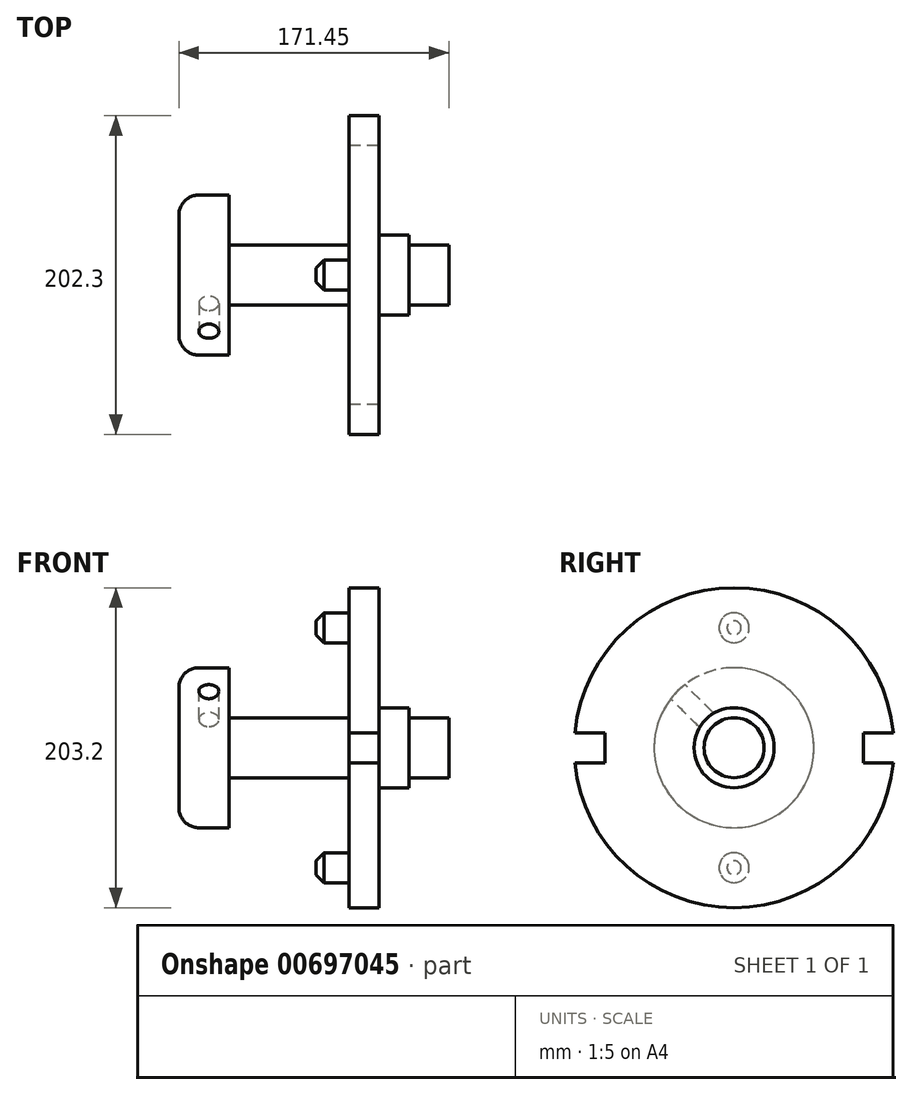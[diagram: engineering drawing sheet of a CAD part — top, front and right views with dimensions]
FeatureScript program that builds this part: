
annotation { "Feature Type Name" : "Feature", "Feature Type Description" : "" }
export const myFeature = defineFeature(function(context is Context, id is Id, definition is map)
    precondition{}
    {
        {
            var Q0;
            Q0=qCreatedBy(makeId("Front.planeOp"),FACE);
            var sketch = newSketch(context, id + "F0", { "sketchPlane" : qUnion([Q0])});
            skLineSegment(sketch, "E0", {"start": v(-314.96, 0) * mm, "end": v(248.68, 0) * mm, "construction": true});
            skLineSegment(sketch, "E1", {"start": v(0, 0) * mm, "end": v(0, 19.05) * mm});
            skLineSegment(sketch, "E2", {"start": v(0, 19.05) * mm, "end": v(-25.4, 19.05) * mm});
            skLineSegment(sketch, "E3", {"start": v(-25.4, 19.05) * mm, "end": v(-25.4, 25.4) * mm});
            skLineSegment(sketch, "E4", {"start": v(-25.4, 25.4) * mm, "end": v(-44.45, 25.4) * mm});
            skLineSegment(sketch, "E5", {"start": v(-44.45, 25.4) * mm, "end": v(-44.45, 101.6) * mm});
            skLineSegment(sketch, "E6", {"start": v(-44.45, 101.6) * mm, "end": v(-63.5, 101.6) * mm});
            skLineSegment(sketch, "E7", {"start": v(-63.5, 101.6) * mm, "end": v(-63.5, 19.05) * mm});
            skLineSegment(sketch, "E8", {"start": v(-63.5, 19.05) * mm, "end": v(-139.7, 19.05) * mm});
            skLineSegment(sketch, "E9", {"start": v(-139.7, 19.05) * mm, "end": v(-139.7, 50.8) * mm});
            skLineSegment(sketch, "E10", {"start": v(-139.7, 50.8) * mm, "end": v(-158.75, 50.8) * mm});
            skLineSegment(sketch, "E11", {"start": v(-171.45, 38.1) * mm, "end": v(-171.45, 0) * mm});
            skPoint(sketch, "E12.visualSharp", {"position": v(-171.45, 50.8) * mm});
            skArc(sketch, "E12.filletArc", {"start": v(-158.75, 50.8) * mm, "mid": v(-167.73, 47.08) * mm, "end": v(-171.45, 38.1) * mm});
            skLineSegment(sketch, "E13", {"start": v(-171.45, 0) * mm, "end": v(0, 0) * mm});
            skSolve(sketch);
        }
        {
            var Q0;
            Q0=makeQuery(id+"F0.imprint","IMPRINT",FACE,{"disambiguationData":[TD([[makeQuery(id+"F0.imprint","IMPRINT",EDGE,{"derivedFrom":sQuery(id+"F0.wireOp",EDGE,"E1")}),1.0]])]});
            var Q1;
            Q1=sQuery(id+"F0.wireOp",EDGE,"E0");
            revolve(context, id + "F1", {"entities" : qUnion([Q0]), "axis" : qUnion([Q1]), "revolveType" : RevolveType.FULL});
        }
        {
            var Q0;
            Q0=makeQuery(id+"F1.opRevolve","SWEPT_FACE",FACE,{"disambiguationData":[OSD([sQuery(id+"F0.wireOp",EDGE,"E7")])]});
            var sketch = newSketch(context, id + "F2", { "sketchPlane" : qUnion([Q0])});
            skLineSegment(sketch, "E14", {"start": v(0, 101.6) * mm, "end": v(0, -101.6) * mm, "construction": true});
            skCircle(sketch, "E15", {"center": v(0, 76.2) * mm, "radius": 9.53 * mm});
            skSolve(sketch);
        }
        {
            var Q0;
            Q0=makeQuery(id+"F2.imprint","IMPRINT",FACE,{"disambiguationData":[TD([[makeQuery(id+"F2.imprint","IMPRINT",EDGE,{"derivedFrom":sQuery(id+"F2.wireOp",EDGE,"E15")}),1.0]])]});
            extrude(context, id + "F3", {"entities" : qUnion([Q0]), "operationType" : NewBodyOperationType.ADD, "depth" : 20.83 * mm});
        }
        {
            var Q0;
            Q0=makeQuery(id+"F3.opExtrude","CAP_EDGE",EDGE,{"disambiguationData":[OSD([sQuery(id+"F2.wireOp",EDGE,"E15")])],"isStart":false});
            chamfer(context, id + "F4", {"entities" : qUnion([Q0]), "width" : 5.08 * mm, "tangentPropagation" : true});
        }
        {
            var Q0;
            Q0=makeQuery(id+"F1.opRevolve","SWEPT_FACE",FACE,{"disambiguationData":[OSD([sQuery(id+"F0.wireOp",EDGE,"E7")])]});
            var sketch = newSketch(context, id + "F5", { "sketchPlane" : qUnion([Q0])});
            skLineSegment(sketch, "E16", {"start": v(0, -101.6) * mm, "end": v(0, 0) * mm, "construction": true});
            skCircle(sketch, "E17", {"center": v(0, -76.2) * mm, "radius": 9.53 * mm});
            skSolve(sketch);
        }
        {
            var Q0;
            Q0=makeQuery(id+"F5.imprint","IMPRINT",FACE,{"disambiguationData":[TD([[makeQuery(id+"F5.imprint","IMPRINT",EDGE,{"derivedFrom":sQuery(id+"F5.wireOp",EDGE,"E17")}),1.0]])]});
            extrude(context, id + "F6", {"entities" : qUnion([Q0]), "operationType" : NewBodyOperationType.ADD, "depth" : 20.83 * mm});
        }
        {
            var Q0;
            Q0=makeQuery(id+"F6.opExtrude","CAP_EDGE",EDGE,{"disambiguationData":[OSD([sQuery(id+"F5.wireOp",EDGE,"E17")])],"isStart":false});
            chamfer(context, id + "F7", {"entities" : qUnion([Q0]), "width" : 5.08 * mm, "tangentPropagation" : true});
        }
        {
            var Q0;
            Q0=makeQuery(id+"F1.opRevolve","SWEPT_FACE",FACE,{"disambiguationData":[OSD([sQuery(id+"F0.wireOp",EDGE,"E7")])]});
            var sketch = newSketch(context, id + "F8", { "sketchPlane" : qUnion([Q0])});
            skLineSegment(sketch, "E18", {"start": v(-101.6, 0) * mm, "end": v(0, 0) * mm, "construction": true});
            skLineSegment(sketch, "E19", {"start": v(-101.15, 9.53) * mm, "end": v(-82.1, 9.53) * mm});
            skLineSegment(sketch, "E20", {"start": v(-82.1, 9.53) * mm, "end": v(-82.1, -9.53) * mm});
            skLineSegment(sketch, "E21", {"start": v(-82.1, -9.53) * mm, "end": v(-101.15, -9.53) * mm});
            skSolve(sketch);
        }
        {
            var Q0;
            {var subQ0=sQuery(id+"F8.wireOp",EDGE,"E19");Q0=makeQuery(id+"F8.imprint","IMPRINT",FACE,{"disambiguationData":[TD([[makeQuery(id+"F8.imprint","IMPRINT",EDGE,{"derivedFrom":subQ0}),-1.0]])]});}
            extrude(context, id + "F9", {"entities" : qUnion([Q0]), "operationType" : NewBodyOperationType.REMOVE, "oppositeDirection" : true, "depth" : 25.4 * mm});
        }
        {
            var Q0;
            Q0=makeQuery(id+"F1.opRevolve","SWEPT_FACE",FACE,{"disambiguationData":[OSD([sQuery(id+"F0.wireOp",EDGE,"E7")])]});
            var sketch = newSketch(context, id + "F10", { "sketchPlane" : qUnion([Q0])});
            skLineSegment(sketch, "E22", {"start": v(0, 0) * mm, "end": v(101.6, 0) * mm, "construction": true});
            skLineSegment(sketch, "E23", {"start": v(101.15, 9.53) * mm, "end": v(82.1, 9.53) * mm});
            skLineSegment(sketch, "E24", {"start": v(82.1, 9.53) * mm, "end": v(82.1, -9.52) * mm});
            skLineSegment(sketch, "E25", {"start": v(82.1, -9.52) * mm, "end": v(101.6, -9.52) * mm});
            skSolve(sketch);
        }
        {
            var Q0;
            {var subQ0=sQuery(id+"F10.wireOp",EDGE,"E23");Q0=makeQuery(id+"F10.imprint","IMPRINT",FACE,{"disambiguationData":[TD([[makeQuery(id+"F10.imprint","IMPRINT",EDGE,{"derivedFrom":subQ0}),1.0]])]});}
            extrude(context, id + "F11", {"entities" : qUnion([Q0]), "operationType" : NewBodyOperationType.REMOVE, "oppositeDirection" : true, "depth" : 25.4 * mm});
        }
        {
            var Q0;
            Q0=makeQuery(id+"F1.opRevolve","SWEPT_FACE",FACE,{"disambiguationData":[OSD([sQuery(id+"F0.wireOp",EDGE,"E9")])]});
            var sketch = newSketch(context, id + "F12", { "sketchPlane" : qUnion([Q0])});
            skLineSegment(sketch, "E26", {"start": v(0, 0) * mm, "end": v(-35.92, 35.92) * mm});
            skLineSegment(sketch, "E27", {"start": v(0, -64.38) * mm, "end": v(0, 24.9) * mm});
            skSolve(sketch);
        }
        {
            var Q0;
            Q0=sQuery(id+"F12.wireOp",VERTEX,"E26.end");
            var Q1;
            Q1=sQuery(id+"F12.wireOp",EDGE,"E26");
            cPlane(context, id + "F13", {"entities" : qUnion([Q0, Q1]), "cplaneType" : CPlaneType.LINE_POINT, "offset" : 25.4 * mm, "width" : 152.4 * mm, "height" : 152.4 * mm});
        }
        {
            var Q0;
            Q0=qCreatedBy(id+"F13.planeOp",FACE);
            var sketch = newSketch(context, id + "F14", { "sketchPlane" : qUnion([Q0])});
            skCircle(sketch, "E28", {"center": v(-152.4, 0) * mm, "radius": 6.35 * mm});
            skSolve(sketch);
        }
        {
            var Q0;
            Q0=makeQuery(id+"F14.imprint","IMPRINT",FACE,{"disambiguationData":[TD([[makeQuery(id+"F14.imprint","IMPRINT",EDGE,{"derivedFrom":sQuery(id+"F14.wireOp",EDGE,"E28")}),1.0]])]});
            extrude(context, id + "F15", {"entities" : qUnion([Q0]), "operationType" : NewBodyOperationType.REMOVE, "oppositeDirection" : true, "depth" : 25.4 * mm});
        }
    });
